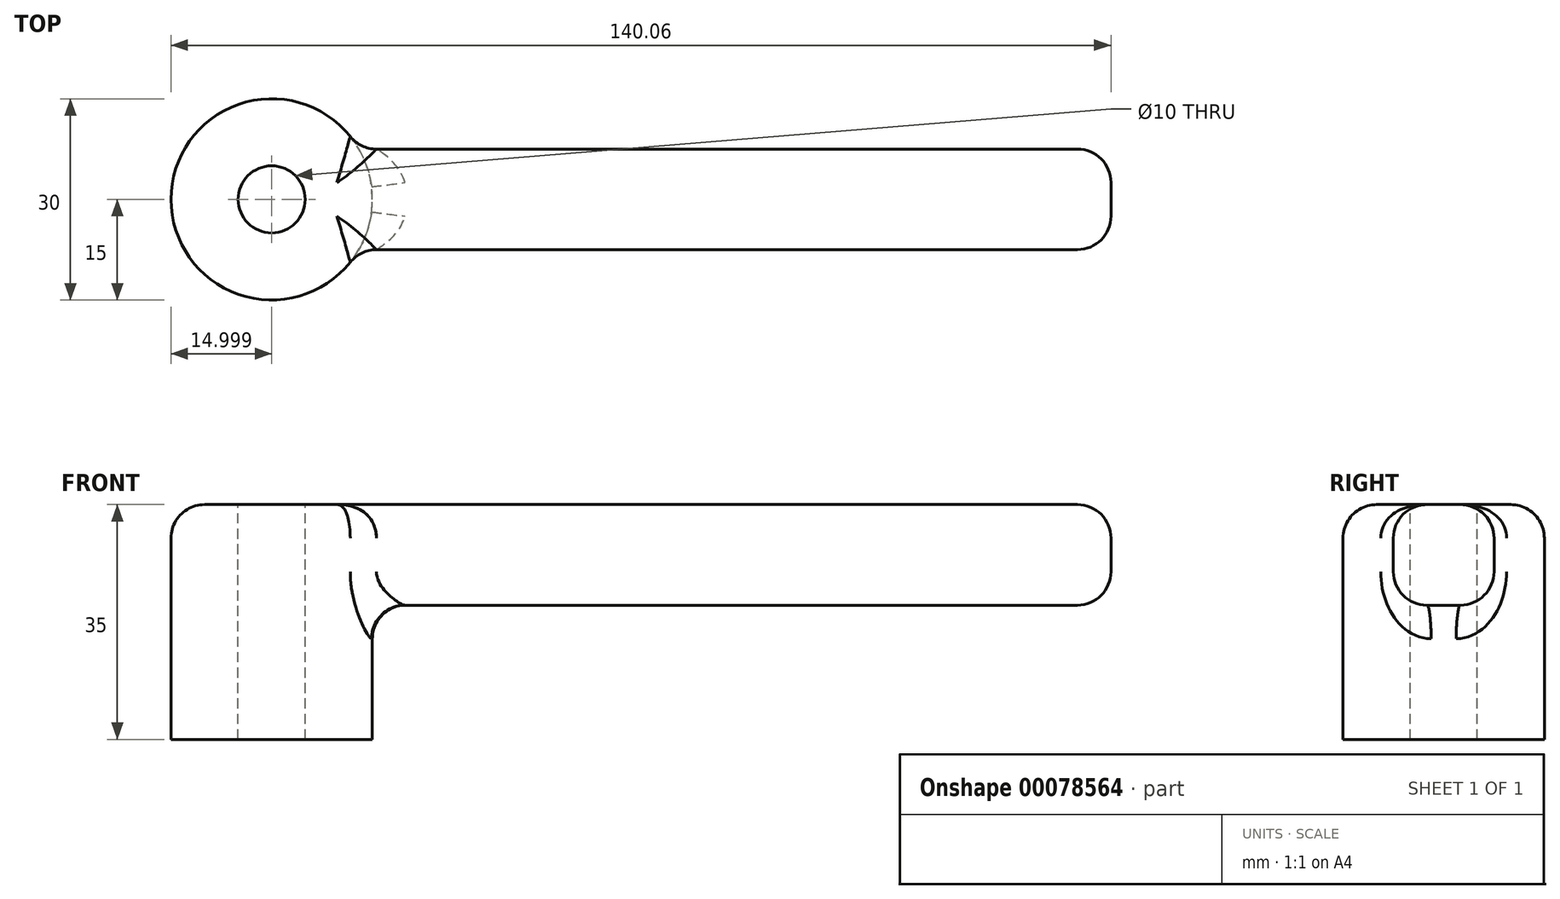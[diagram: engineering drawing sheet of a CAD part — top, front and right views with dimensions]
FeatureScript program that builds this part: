
annotation { "Feature Type Name" : "Feature", "Feature Type Description" : "" }
export const myFeature = defineFeature(function(context is Context, id is Id, definition is map)
    precondition{}
    {
        {
            var Q0;
            Q0=qCreatedBy(makeId("Front.planeOp"),FACE);
            var sketch = newSketch(context, id + "F5", { "sketchPlane" : qUnion([Q0])});
            skLineSegment(sketch, "E0.bottom", {"start": v(32.15, 45.89) * mm, "end": v(-77.91, 45.89) * mm});
            skLineSegment(sketch, "E0.top", {"start": v(32.15, 30.89) * mm, "end": v(-87.85, 30.89) * mm});
            skLineSegment(sketch, "E0.left", {"start": v(32.15, 45.89) * mm, "end": v(32.15, 30.89) * mm});
            skLineSegment(sketch, "E0.right", {"start": v(-87.85, 45.89) * mm, "end": v(-87.85, 30.89) * mm});
            skLineSegment(sketch, "E1.bottom", {"start": v(-77.91, 45.89) * mm, "end": v(-87.91, 45.89) * mm});
            skLineSegment(sketch, "E1.top", {"start": v(-77.91, 10.89) * mm, "end": v(-87.91, 10.89) * mm});
            skLineSegment(sketch, "E1.left", {"start": v(-77.91, 45.89) * mm, "end": v(-77.91, 10.89) * mm});
            skLineSegment(sketch, "E1.right", {"start": v(-87.91, 45.89) * mm, "end": v(-87.91, 10.89) * mm});
            skLineSegment(sketch, "E2.bottom", {"start": v(-82.91, 45.89) * mm, "end": v(-82.91, 45.89) * mm});
            skLineSegment(sketch, "E2.top", {"start": v(-82.91, 45.89) * mm, "end": v(-82.91, 45.89) * mm});
            skLineSegment(sketch, "E2.left", {"start": v(-82.91, 45.89) * mm, "end": v(-82.91, 45.89) * mm});
            skLineSegment(sketch, "E2.right", {"start": v(-82.91, 45.89) * mm, "end": v(-82.91, 45.89) * mm});
            skLineSegment(sketch, "E3", {"start": v(-92.91, 45.89) * mm, "end": v(-92.91, 10.89) * mm});
            skSolve(sketch);
        }
        {
            var Q0;
            {var subQ5=sQuery(id+"F5.wireOp",EDGE,"E1.bottom");Q0=makeQuery(id+"F5.imprint","IMPRINT",FACE,{"disambiguationData":[TD([[makeQuery(id+"F5.imprint","IMPRINT",EDGE,{"derivedFrom":subQ5}),1.0]])]});}
            var Q1;
            {var subQ0=sQuery(id+"F5.wireOp",EDGE,"E0.bottom");Q1=makeQuery(id+"F5.imprint","IMPRINT",FACE,{"disambiguationData":[TD([[makeQuery(id+"F5.imprint","IMPRINT",EDGE,{"derivedFrom":subQ0}),1.0]])]});}
            extrude(context, id + "F0", {"entities" : qUnion([Q0, Q1]), "endBound" : BoundingType.SYMMETRIC, "depth" : 15 * mm});
        }
        {
            var Q0;
            {var subQ5=sQuery(id+"F5.wireOp",EDGE,"E1.bottom");Q0=makeQuery(id+"F5.imprint","IMPRINT",FACE,{"disambiguationData":[TD([[makeQuery(id+"F5.imprint","IMPRINT",EDGE,{"derivedFrom":subQ5}),1.0]])]});}
            var Q1;
            {var subQ5=sQuery(id+"F5.wireOp",EDGE,"E1.top");Q1=makeQuery(id+"F5.imprint","IMPRINT",FACE,{"disambiguationData":[TD([[makeQuery(id+"F5.imprint","IMPRINT",EDGE,{"derivedFrom":subQ5}),-1.0]])]});}
            var Q2;
            Q2=sQuery(id+"F5.wireOp",EDGE,"E3");
            revolve(context, id + "F1", {"entities" : qUnion([Q0, Q1]), "axis" : qUnion([Q2]), "revolveType" : RevolveType.FULL});
        }
        {
            var Q0;
            Q0=makeQuery(id+"F0.opExtrude","CAP_EDGE",EDGE,{"disambiguationData":[OSD([sQuery(id+"F5.wireOp",EDGE,"E0.left")])],"isStart":false});
            var Q1;
            Q1=makeQuery(id+"F0.opExtrude","CAP_EDGE",EDGE,{"disambiguationData":[OSD([sQuery(id+"F5.wireOp",EDGE,"E0.left")])],"isStart":true});
            var Q2;
            Q2=makeQuery(id+"F0.opExtrude","SWEPT_EDGE",EDGE,{"disambiguationData":[OSD([sQuery(id+"F5.wireOp",EDGE,"E0.bottom"),sQuery(id+"F5.wireOp",EDGE,"E0.left")])]});
            var Q3;
            Q3=makeQuery(id+"F0.opExtrude","SWEPT_FACE",FACE,{"disambiguationData":[OSD([sQuery(id+"F5.wireOp",EDGE,"E0.left")])]});
            var Q4;
            Q4=makeQuery(id+"F0.opExtrude","CAP_EDGE",EDGE,{"disambiguationData":[OSD([sQuery(id+"F5.wireOp",EDGE,"E0.bottom"),sQuery(id+"F5.wireOp",EDGE,"E1.bottom")])],"isStart":false});
            var Q5;
            Q5=makeQuery(id+"F0.opExtrude","CAP_EDGE",EDGE,{"disambiguationData":[OSD([sQuery(id+"F5.wireOp",EDGE,"E0.top")])],"isStart":false});
            var Q6;
            Q6=makeQuery(id+"F0.opExtrude","CAP_EDGE",EDGE,{"disambiguationData":[OSD([sQuery(id+"F5.wireOp",EDGE,"E0.bottom"),sQuery(id+"F5.wireOp",EDGE,"E1.bottom")])],"isStart":true});
            var Q7;
            Q7=makeQuery(id+"F0.opExtrude","CAP_EDGE",EDGE,{"disambiguationData":[OSD([sQuery(id+"F5.wireOp",EDGE,"E0.top")])],"isStart":true});
            var Q8;
            Q8=makeQuery(id+"F1.opRevolve","SWEPT_EDGE",EDGE,{"disambiguationData":[OSD([sQuery(id+"F5.wireOp",EDGE,"E0.bottom"),sQuery(id+"F5.wireOp",EDGE,"E1.bottom"),sQuery(id+"F5.wireOp",EDGE,"E1.left")])]});
            fillet(context, id + "F2", {"entities" : qUnion([Q0, Q1, Q2, Q3, Q4, Q5, Q6, Q7, Q8]), "radius" : 5 * mm, "tangentPropagation" : true, "allowEdgeOverflow" : false});
        }
        {
            var Q0;
            Q0=makeQuery(id+"F1.opRevolve","SWEPT_BODY",BODY,{"disambiguationData":[OSD([sQuery(id+"F5.wireOp",EDGE,"E1.bottom"),sQuery(id+"F5.wireOp",EDGE,"E1.top"),sQuery(id+"F5.wireOp",EDGE,"E1.left"),sQuery(id+"F5.wireOp",EDGE,"E1.right")])]});
            var Q1;
            Q1=makeQuery(id+"F0.opExtrude","SWEPT_BODY",BODY,{"disambiguationData":[OSD([sQuery(id+"F5.wireOp",EDGE,"E0.bottom"),sQuery(id+"F5.wireOp",EDGE,"E0.top"),sQuery(id+"F5.wireOp",EDGE,"E0.left"),sQuery(id+"F5.wireOp",EDGE,"E1.bottom"),sQuery(id+"F5.wireOp",EDGE,"E1.right")])]});
            booleanBodies(context, id + "F3", {"operationType" : BooleanOperationType.UNION, "tools" : qUnion([Q0, Q1])});
        }
        {
            var Q0;
            Q0=makeQuery(id+"F3.opBoolean","INTERSECT",EDGE,{"derivedFrom":[makeQuery(id+"F0.opExtrude","CAP_FACE",FACE,{"disambiguationData":[OSD([sQuery(id+"F5.wireOp",EDGE,"E0.bottom"),sQuery(id+"F5.wireOp",EDGE,"E0.top"),sQuery(id+"F5.wireOp",EDGE,"E0.left"),sQuery(id+"F5.wireOp",EDGE,"E1.bottom"),sQuery(id+"F5.wireOp",EDGE,"E1.right")])],"isStart":false}),makeQuery(id+"F1.opRevolve","SWEPT_FACE",FACE,{"disambiguationData":[OSD([sQuery(id+"F5.wireOp",EDGE,"E1.left")])]})]});
            var Q1;
            Q1=makeQuery(id+"F3.opBoolean","INTERSECT",EDGE,{"derivedFrom":[makeQuery(id+"F0.opExtrude","CAP_FACE",FACE,{"disambiguationData":[OSD([sQuery(id+"F5.wireOp",EDGE,"E0.bottom"),sQuery(id+"F5.wireOp",EDGE,"E0.top"),sQuery(id+"F5.wireOp",EDGE,"E0.left"),sQuery(id+"F5.wireOp",EDGE,"E1.bottom"),sQuery(id+"F5.wireOp",EDGE,"E1.right")])],"isStart":true}),makeQuery(id+"F1.opRevolve","SWEPT_FACE",FACE,{"disambiguationData":[OSD([sQuery(id+"F5.wireOp",EDGE,"E1.left")])]})]});
            fillet(context, id + "F4", {"entities" : qUnion([Q0, Q1]), "radius" : 5 * mm, "tangentPropagation" : true, "allowEdgeOverflow" : false});
        }
    });
